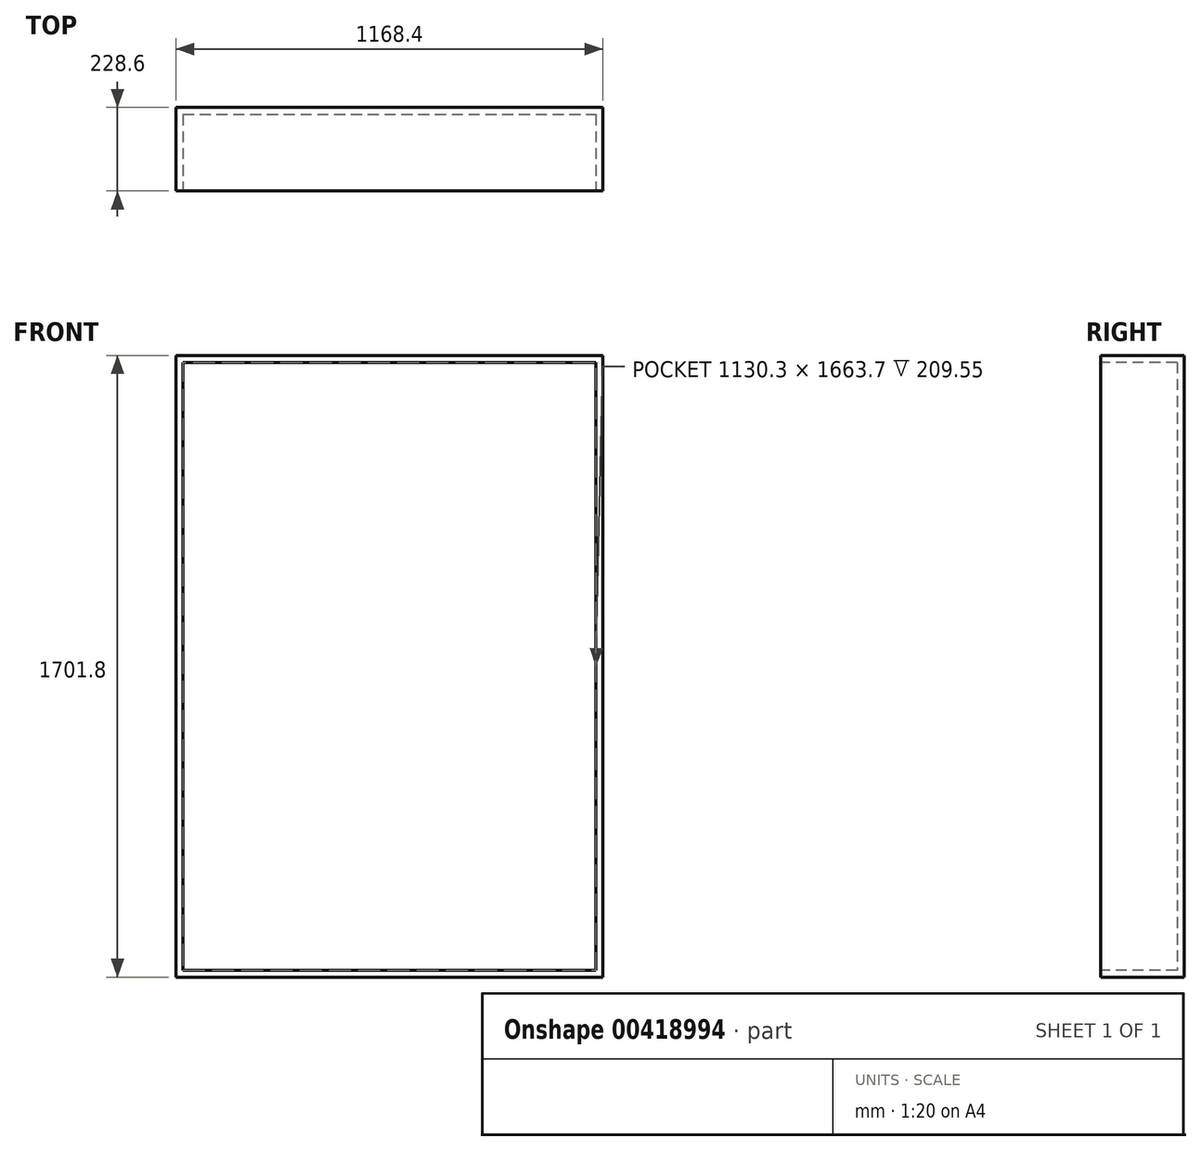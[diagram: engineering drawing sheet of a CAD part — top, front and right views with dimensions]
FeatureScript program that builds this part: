
annotation { "Feature Type Name" : "Feature", "Feature Type Description" : "" }
export const myFeature = defineFeature(function(context is Context, id is Id, definition is map)
    precondition{}
    {
        {
            var Q0;
            Q0=qCreatedBy(makeId("Front.planeOp"),FACE);
            var sketch = newSketch(context, id + "F0", { "sketchPlane" : qUnion([Q0])});
            skLineSegment(sketch, "E0.bottom", {"start": v(-584.2, 1701.8) * mm, "end": v(584.2, 1701.8) * mm});
            skLineSegment(sketch, "E0.top", {"start": v(-584.2, 0) * mm, "end": v(584.2, 0) * mm});
            skLineSegment(sketch, "E0.left", {"start": v(-584.2, 1701.8) * mm, "end": v(-584.2, 0) * mm});
            skLineSegment(sketch, "E0.right", {"start": v(584.2, 1701.8) * mm, "end": v(584.2, 0) * mm});
            skLineSegment(sketch, "E1.bottom", {"start": v(584.2, 1701.8) * mm, "end": v(584.2, 1701.8) * mm});
            skLineSegment(sketch, "E1.top", {"start": v(584.2, 1701.8) * mm, "end": v(584.2, 1701.8) * mm});
            skLineSegment(sketch, "E1.left", {"start": v(584.2, 1701.8) * mm, "end": v(584.2, 1701.8) * mm});
            skLineSegment(sketch, "E1.right", {"start": v(584.2, 1701.8) * mm, "end": v(584.2, 1701.8) * mm});
            skSolve(sketch);
        }
        {
            var Q0;
            Q0 = qSketchRegion(id + "F0", true);
            extrude(context, id + "F1", {"entities" : qUnion([Q0]), "depth" : 228.6 * mm});
        }
        {
            var Q0;
            Q0=makeQuery(id+"F1.opExtrude","CAP_FACE",FACE,{"disambiguationData":[OSD([sQuery(id+"F0.wireOp",EDGE,"E0.bottom"),sQuery(id+"F0.wireOp",EDGE,"E0.top"),sQuery(id+"F0.wireOp",EDGE,"E0.left"),sQuery(id+"F0.wireOp",EDGE,"E0.right")])],"isStart":false});
            var sketch = newSketch(context, id + "F2", { "sketchPlane" : qUnion([Q0])});
            skLineSegment(sketch, "E2.bottom", {"start": v(-565.15, 1682.75) * mm, "end": v(565.15, 1682.75) * mm});
            skLineSegment(sketch, "E2.top", {"start": v(-565.15, 19.05) * mm, "end": v(565.15, 19.05) * mm});
            skLineSegment(sketch, "E2.left", {"start": v(-565.15, 1682.75) * mm, "end": v(-565.15, 19.05) * mm});
            skLineSegment(sketch, "E2.right", {"start": v(565.15, 1682.75) * mm, "end": v(565.15, 19.05) * mm});
            skSolve(sketch);
        }
        {
            var Q0;
            Q0=makeQuery(id+"F2.imprint","IMPRINT",FACE,{"disambiguationData":[TD([[makeQuery(id+"F2.imprint","IMPRINT",EDGE,{"derivedFrom":sQuery(id+"F2.wireOp",EDGE,"E2.bottom")}),-1.0]])]});
            extrude(context, id + "F3", {"entities" : qUnion([Q0]), "operationType" : NewBodyOperationType.REMOVE, "oppositeDirection" : true, "depth" : 209.55 * mm});
        }
    });
